# Revit family: Cable management panel
name_source: partatom
category: Equipement spécialisé
units: mm (PartAtom-declared; Revit-internal decimal feet)

## family parameters
Basée sur le plan de construction = Non
Cote de connecteur circulaire = Utiliser le diamètre
Couper avec des vides une fois chargée = Non
Partagée = Oui
Point de calcul de pièce = Non
Toujours verticalement = Oui
Type d'élément = Normal

## types (1)
- Enclosures accessories Legrand
    Application class = EC000322
    BIM wording = Enclosures accessories Legrand
    Color = IDS_NOIR
    Depth (mm) = 90 mm  [stored 0.295276 ft]
    E-catalogue link = https://www.legrand.fr
    EAN = 3245060465223
    Elévation par défaut = 0 mm  [stored 0 ft]
    Function = Cable management
    Legrand part number = 046522
    Length = 385
    Material = Metal
    Model = Patch panel
    Number of height units = 1
    RAL Number = 9005
    Width (mm) = 482 mm  [stored 1.58136 ft]

note: [stored X ft] marks values corroborated as IEEE doubles in the binary element streams (Revit-internal decimal feet)
